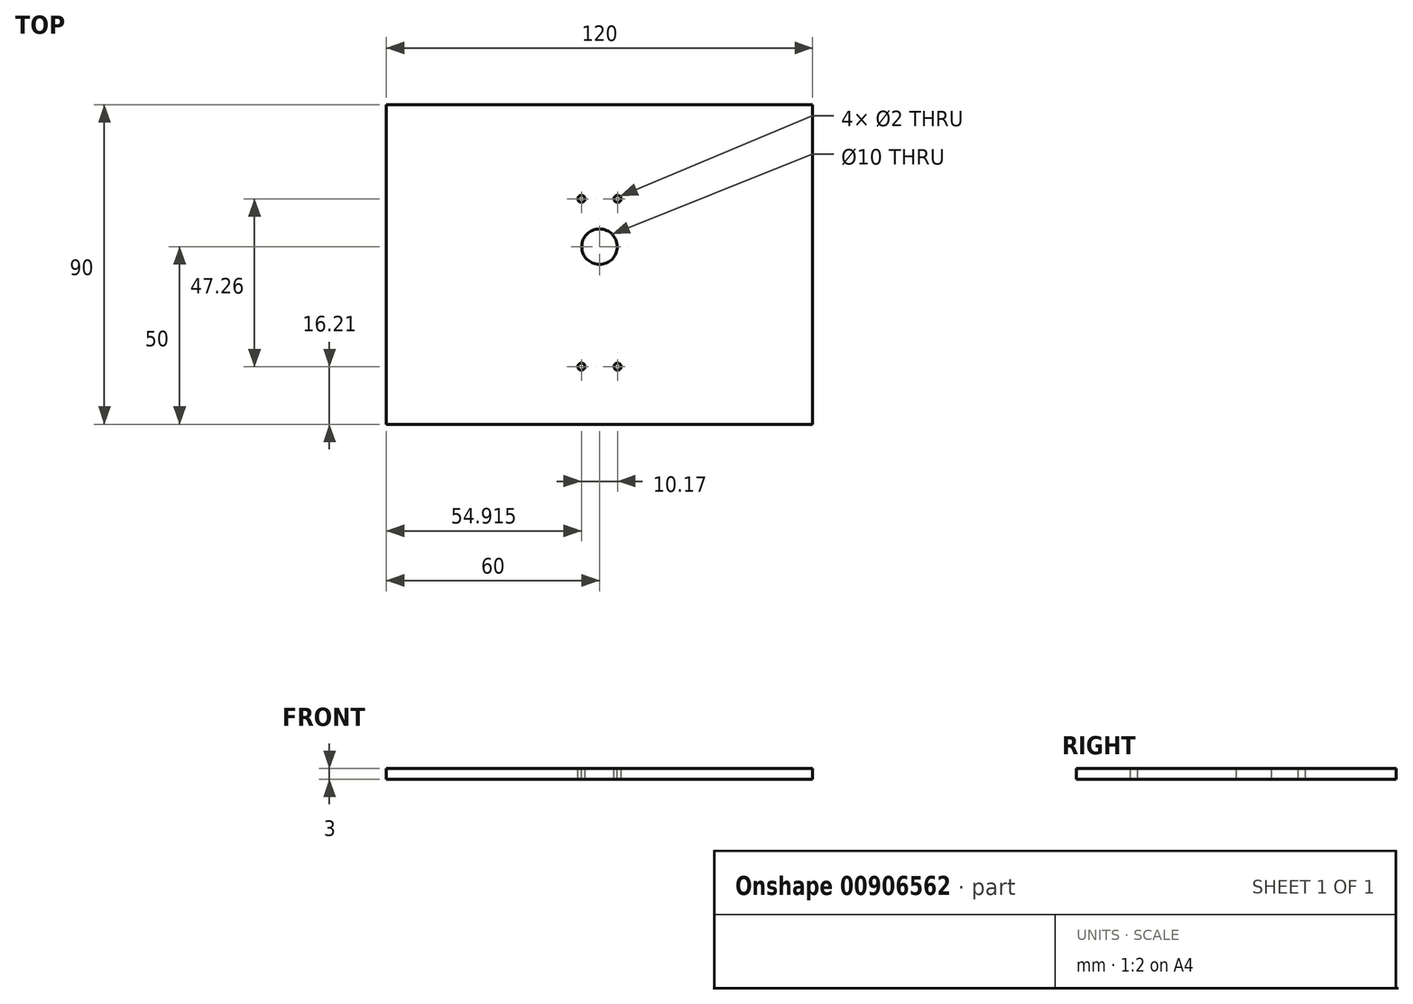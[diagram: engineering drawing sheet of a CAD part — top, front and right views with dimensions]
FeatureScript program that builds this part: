
annotation { "Feature Type Name" : "Feature", "Feature Type Description" : "" }
export const myFeature = defineFeature(function(context is Context, id is Id, definition is map)
    precondition{}
    {
        {
            var Q0;
            Q0=qCreatedBy(makeId("Top.planeOp"),FACE);
            var sketch = newSketch(context, id + "F0", { "sketchPlane" : qUnion([Q0])});
            skLineSegment(sketch, "E0.bottom", {"start": v(-60, 45) * mm, "end": v(60, 45) * mm});
            skLineSegment(sketch, "E0.top", {"start": v(-60, -45) * mm, "end": v(60, -45) * mm});
            skLineSegment(sketch, "E0.left", {"start": v(-60, 45) * mm, "end": v(-60, -45) * mm});
            skLineSegment(sketch, "E0.right", {"start": v(60, 45) * mm, "end": v(60, -45) * mm});
            skPoint(sketch, "E0.middle", {"position": v(0, 0) * mm});
            skCircle(sketch, "E1", {"center": v(0, -5) * mm, "radius": 5 * mm});
            skCircle(sketch, "E2", {"center": v(5.1, -18.47) * mm, "radius": 1 * mm});
            skCircle(sketch, "E3", {"center": v(-5.08, -18.47) * mm, "radius": 1 * mm});
            skCircle(sketch, "E4", {"center": v(-5.09, 28.79) * mm, "radius": 1 * mm});
            skCircle(sketch, "E5", {"center": v(5.1, 28.79) * mm, "radius": 1 * mm});
            skSolve(sketch);
        }
        {
            var Q0;
            Q0 = qSketchRegion(id + "F0", true);
            var Q1;
            Q1=makeQuery(id+"F0.imprint","IMPRINT",FACE,{"disambiguationData":[TD([[makeQuery(id+"F0.imprint","IMPRINT",EDGE,{"derivedFrom":sQuery(id+"F0.wireOp",EDGE,"E1")}),1.0]])]});
            var Q2;
            Q2=makeQuery(id+"F0.imprint","IMPRINT",FACE,{"disambiguationData":[TD([[makeQuery(id+"F0.imprint","IMPRINT",EDGE,{"derivedFrom":sQuery(id+"F0.wireOp",EDGE,"E5")}),1.0]])]});
            var Q3;
            Q3=makeQuery(id+"F0.imprint","IMPRINT",FACE,{"disambiguationData":[TD([[makeQuery(id+"F0.imprint","IMPRINT",EDGE,{"derivedFrom":sQuery(id+"F0.wireOp",EDGE,"E4")}),1.0]])]});
            var Q4;
            Q4=makeQuery(id+"F0.imprint","IMPRINT",FACE,{"disambiguationData":[TD([[makeQuery(id+"F0.imprint","IMPRINT",EDGE,{"derivedFrom":sQuery(id+"F0.wireOp",EDGE,"E3")}),1.0]])]});
            var Q5;
            Q5=makeQuery(id+"F0.imprint","IMPRINT",FACE,{"disambiguationData":[TD([[makeQuery(id+"F0.imprint","IMPRINT",EDGE,{"derivedFrom":sQuery(id+"F0.wireOp",EDGE,"E2")}),1.0]])]});
            extrude(context, id + "F1", {"entities" : qUnion([Q0, Q1, Q2, Q3, Q4, Q5]), "depth" : 3 * mm, "offsetDistance" : 25 * mm});
        }
        {
            var Q0;
            Q0=makeQuery(id+"F1.opExtrude","CAP_FACE",FACE,{"disambiguationData":[OSD([sQuery(id+"F0.wireOp",EDGE,"E0.bottom"),sQuery(id+"F0.wireOp",EDGE,"E0.top"),sQuery(id+"F0.wireOp",EDGE,"E0.left"),sQuery(id+"F0.wireOp",EDGE,"E0.right")])],"isStart":false});
            var sketch = newSketch(context, id + "F2", { "sketchPlane" : qUnion([Q0])});
            skCircle(sketch, "E6", {"center": v(0, 5) * mm, "radius": 5 * mm});
            skCircle(sketch, "E7", {"center": v(5.08, 18.47) * mm, "radius": 1 * mm});
            skCircle(sketch, "E8", {"center": v(-5.08, 18.47) * mm, "radius": 1 * mm});
            skCircle(sketch, "E9", {"center": v(5.08, -28.8) * mm, "radius": 1 * mm});
            skCircle(sketch, "E10", {"center": v(-5.08, -28.8) * mm, "radius": 1 * mm});
            skSolve(sketch);
        }
        {
            var Q0;
            Q0=makeQuery(id+"F2.imprint","IMPRINT",FACE,{"disambiguationData":[TD([[makeQuery(id+"F2.imprint","IMPRINT",EDGE,{"derivedFrom":sQuery(id+"F2.wireOp",EDGE,"E6")}),1.0]])]});
            var Q1;
            Q1=makeQuery(id+"F2.imprint","IMPRINT",FACE,{"disambiguationData":[TD([[makeQuery(id+"F2.imprint","IMPRINT",EDGE,{"derivedFrom":sQuery(id+"F2.wireOp",EDGE,"E9")}),1.0]])]});
            var Q2;
            Q2=makeQuery(id+"F2.imprint","IMPRINT",FACE,{"disambiguationData":[TD([[makeQuery(id+"F2.imprint","IMPRINT",EDGE,{"derivedFrom":sQuery(id+"F2.wireOp",EDGE,"E10")}),1.0]])]});
            var Q3;
            Q3=makeQuery(id+"F2.imprint","IMPRINT",FACE,{"disambiguationData":[TD([[makeQuery(id+"F2.imprint","IMPRINT",EDGE,{"derivedFrom":sQuery(id+"F2.wireOp",EDGE,"E7")}),1.0]])]});
            var Q4;
            Q4=makeQuery(id+"F2.imprint","IMPRINT",FACE,{"disambiguationData":[TD([[makeQuery(id+"F2.imprint","IMPRINT",EDGE,{"derivedFrom":sQuery(id+"F2.wireOp",EDGE,"E8")}),1.0]])]});
            extrude(context, id + "F3", {"entities" : qUnion([Q0, Q1, Q2, Q3, Q4]), "operationType" : NewBodyOperationType.REMOVE, "endBound" : BoundingType.THROUGH_ALL, "oppositeDirection" : true, "depth" : 25 * mm, "offsetDistance" : 25 * mm});
        }
    });
